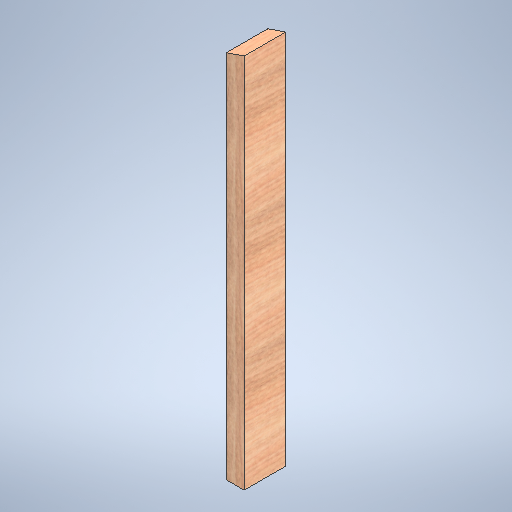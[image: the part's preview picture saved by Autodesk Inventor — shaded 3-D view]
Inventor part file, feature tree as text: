
AUTODESK INVENTOR PART (.ipt)
format: ipt  version: 2025.1 (Build 291241020, 241B)  size: 331,264 bytes
history: native  units: in
note: dims shown in document units (in); Inventor stores cm internally (conversion verified against a paired STEP export)
features: extrude x1, sketch x1
ambient origin geometry x8: Origin, YZ Plane, XZ Plane, XY Plane, X Axis, Y Axis, Z Axis, Center Point
bodies: Solid1 (feature_tree)
feature tree (2):
  extrude  "Extrusion1"  Depth=3.5in TaperAngle=0.0deg
  sketch  "Sketch1"  dims[d2=1.5in d3=3.5in d4=0.0in d5=31.239in d6=31.74in]
